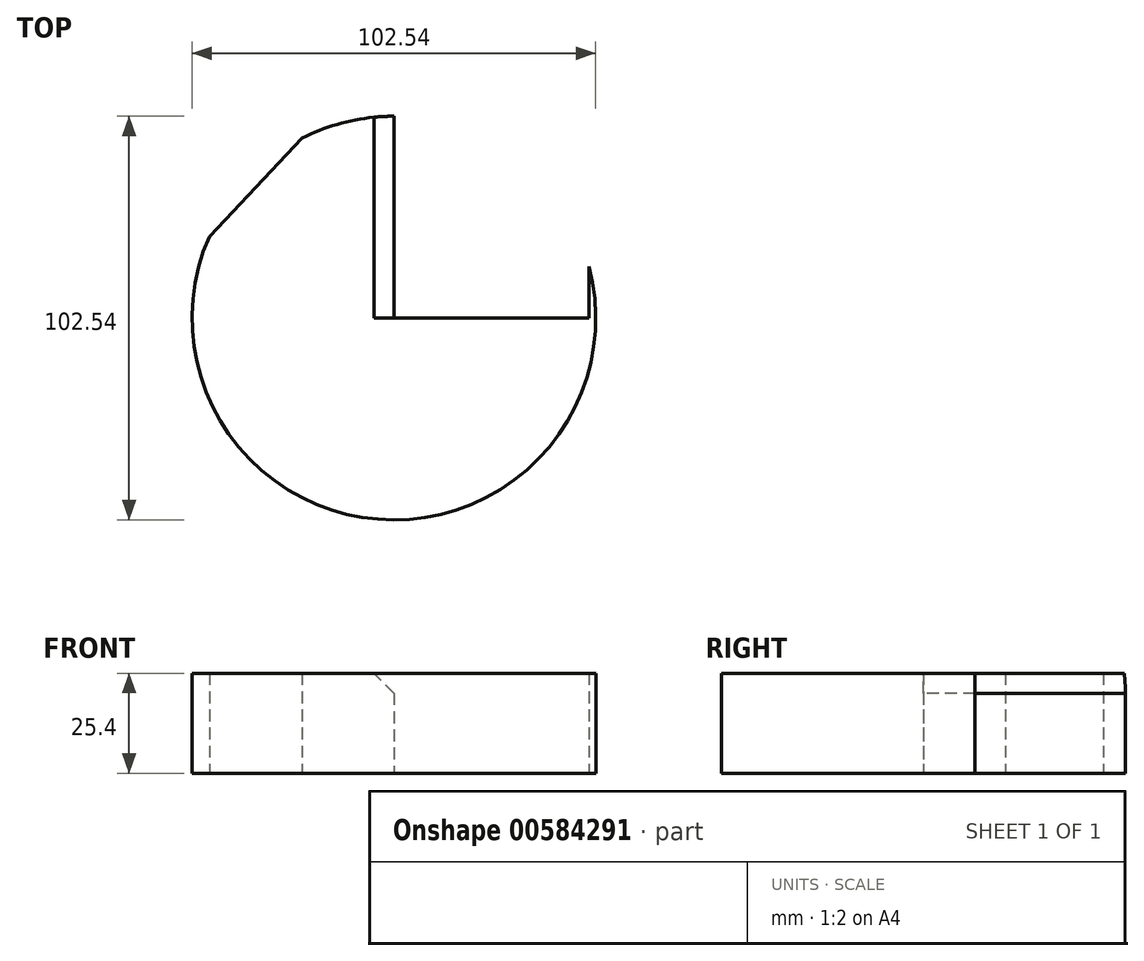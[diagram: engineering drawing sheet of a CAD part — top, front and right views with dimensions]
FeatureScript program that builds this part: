
annotation { "Feature Type Name" : "Feature", "Feature Type Description" : "" }
export const myFeature = defineFeature(function(context is Context, id is Id, definition is map)
    precondition{}
    {
        {
            var Q0;
            Q0=qCreatedBy(makeId("Top.planeOp"),FACE);
            var sketch = newSketch(context, id + "F0", { "sketchPlane" : qUnion([Q0])});
            skCircle(sketch, "E0", {"center": v(0, 0) * mm, "radius": 51.27 * mm});
            skLineSegment(sketch, "E1.bottom", {"start": v(0, 0) * mm, "end": v(49.57, 0) * mm});
            skLineSegment(sketch, "E1.top", {"start": v(0, 70.31) * mm, "end": v(49.57, 70.31) * mm});
            skLineSegment(sketch, "E1.left", {"start": v(0, 0) * mm, "end": v(0, 70.31) * mm});
            skLineSegment(sketch, "E1.right", {"start": v(49.57, 0) * mm, "end": v(49.57, 70.31) * mm});
            skLineSegment(sketch, "E2", {"start": v(0, 70.31) * mm, "end": v(-46.88, 20.76) * mm});
            skSolve(sketch);
        }
        {
            var Q0;
            {var subQ0=sQuery(id+"F0.wireOp",EDGE,"E1.bottom");Q0=makeQuery(id+"F0.imprint","IMPRINT",FACE,{"disambiguationData":[TD([[makeQuery(id+"F0.imprint","IMPRINT",EDGE,{"derivedFrom":subQ0}),-1.0]])]});}
            extrude(context, id + "F1", {"entities" : qUnion([Q0]), "depth" : 25.4 * mm, "offsetDistance" : 25.4 * mm});
        }
        {
            var Q0;
            Q0=makeQuery(id+"F1.opExtrude","CAP_EDGE",EDGE,{"disambiguationData":[OSD([sQuery(id+"F0.wireOp",EDGE,"E1.left")])],"isStart":false});
            chamfer(context, id + "F2", {"entities" : qUnion([Q0]), "width" : 5.08 * mm, "tangentPropagation" : true});
        }
    });
